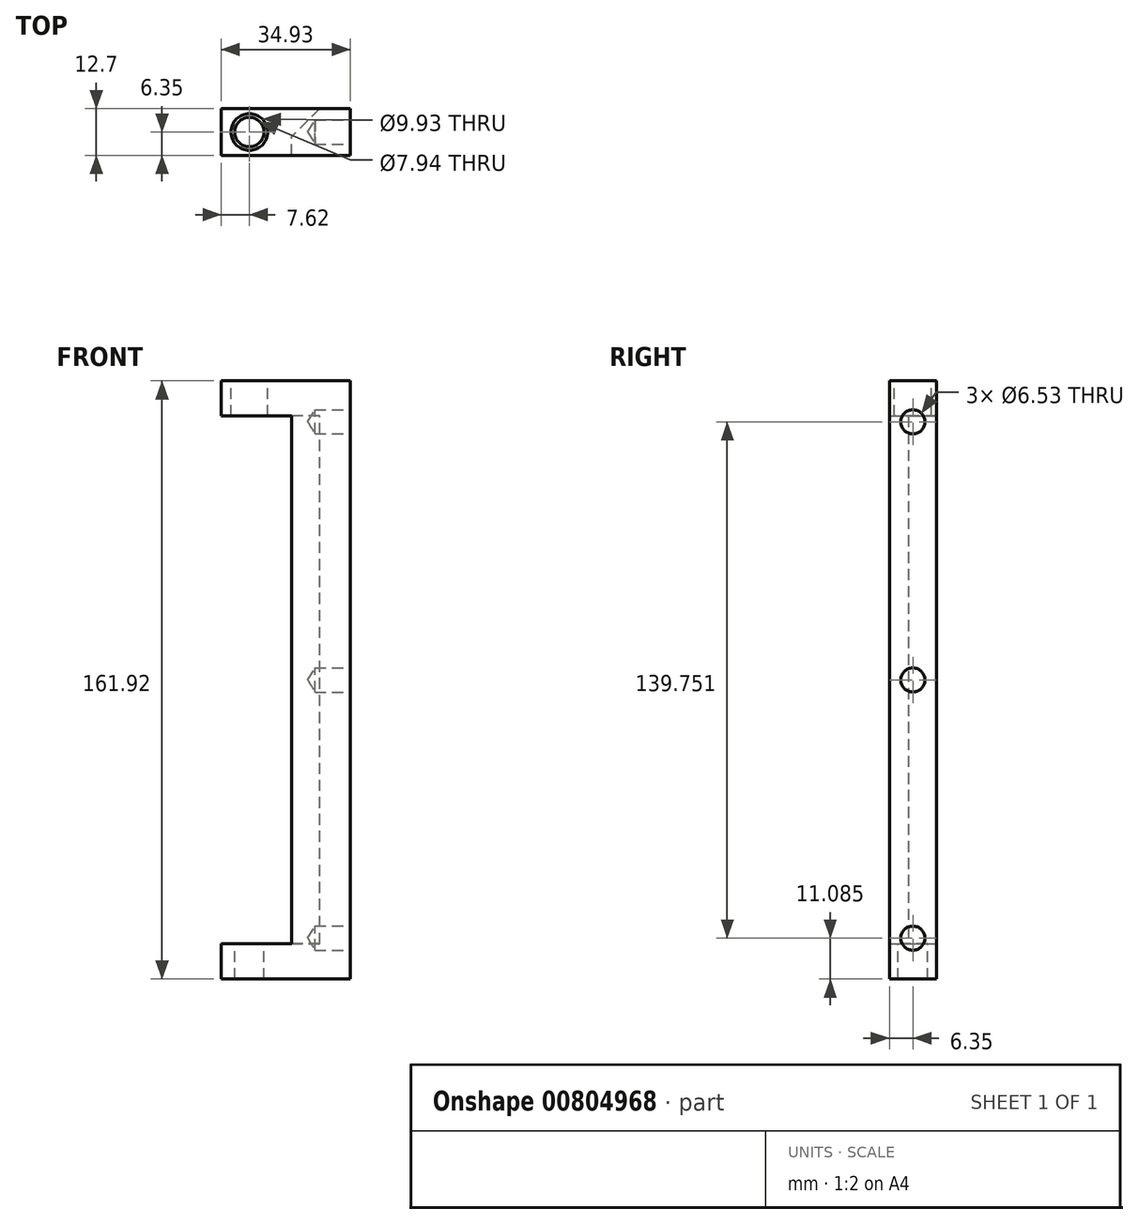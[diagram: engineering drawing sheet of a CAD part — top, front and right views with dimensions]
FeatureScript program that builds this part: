
annotation { "Feature Type Name" : "Feature", "Feature Type Description" : "" }
export const myFeature = defineFeature(function(context is Context, id is Id, definition is map)
    precondition{}
    {
        {
            var Q0;
            Q0=qCreatedBy(makeId("Front.planeOp"),FACE);
            var sketch = newSketch(context, id + "F0", { "sketchPlane" : qUnion([Q0])});
            skLineSegment(sketch, "E0", {"start": v(0, 11.43) * mm, "end": v(0, 71.44) * mm});
            skLineSegment(sketch, "E1", {"start": v(0, 71.44) * mm, "end": v(-19.05, 71.44) * mm});
            skLineSegment(sketch, "E2", {"start": v(-19.05, 71.44) * mm, "end": v(-19.05, 80.96) * mm});
            skLineSegment(sketch, "E3", {"start": v(-19.05, 80.96) * mm, "end": v(15.87, 80.96) * mm});
            skLineSegment(sketch, "E4", {"start": v(15.87, 80.96) * mm, "end": v(15.88, 0) * mm});
            skLineSegment(sketch, "E5", {"start": v(0, 0) * mm, "end": v(15.88, 0) * mm, "construction": true});
            skLineSegment(sketch, "E6.MirrorCS", {"start": v(0, -11.43) * mm, "end": v(0, -71.44) * mm});
            skLineSegment(sketch, "E7.MirrorCS", {"start": v(15.88, -80.96) * mm, "end": v(15.88, 0) * mm});
            skLineSegment(sketch, "E8.MirrorCS", {"start": v(-19.05, -71.44) * mm, "end": v(-19.05, -80.96) * mm});
            skLineSegment(sketch, "E9.MirrorCS", {"start": v(-19.05, -80.96) * mm, "end": v(15.88, -80.96) * mm});
            skLineSegment(sketch, "E10.MirrorCS", {"start": v(0, -71.44) * mm, "end": v(-19.05, -71.44) * mm});
            skLineSegment(sketch, "E11", {"start": v(0, 11.43) * mm, "end": v(-19.05, 11.43) * mm, "construction": true});
            skLineSegment(sketch, "E12", {"start": v(-19.05, 11.43) * mm, "end": v(-19.05, 0) * mm, "construction": true});
            skLineSegment(sketch, "E13.MirrorCS", {"start": v(0, -11.43) * mm, "end": v(-19.05, -11.43) * mm, "construction": true});
            skLineSegment(sketch, "E14.MirrorCS", {"start": v(-19.05, -11.43) * mm, "end": v(-19.05, 0) * mm, "construction": true});
            skPoint(sketch, "E15.orphan", {"position": v(0, 0) * mm});
            skLineSegment(sketch, "E16", {"start": v(0, 11.43) * mm, "end": v(0, -11.43) * mm});
            skSolve(sketch);
        }
        {
            var Q0;
            Q0 = qSketchRegion(id + "F0", true);
            extrude(context, id + "F1", {"entities" : qUnion([Q0]), "depth" : 12.7 * mm, "offsetDistance" : 25.4 * mm});
        }
        {
            var Q0;
            Q0=makeQuery(id+"F1.opExtrude","SWEPT_FACE",FACE,{"disambiguationData":[OSD([sQuery(id+"F0.wireOp",EDGE,"E3")])]});
            var sketch = newSketch(context, id + "F2", { "sketchPlane" : qUnion([Q0])});
            skPoint(sketch, "E17.centerSnap0", {"position": v(-19.05, -6.35) * mm});
            skPoint(sketch, "E18", {"position": v(-11.43, -6.35) * mm});
            skSolve(sketch);
        }
        {
            var Q0;
            Q0=makeQuery(id+"F1.opExtrude","CAP_EDGE",EDGE,{"disambiguationData":[OSD([sQuery(id+"F0.wireOp",EDGE,"E0")])],"isStart":true});
            chamfer(context, id + "F3", {"entities" : qUnion([Q0]), "chamferType" : ChamferType.OFFSET_ANGLE, "width" : 7.62 * mm, "oppositeDirection" : true, "angle" : 45 * degree, "tangentPropagation" : true});
        }
        {
            var Q0;
            Q0=makeQuery(id+"F1.opExtrude","SWEPT_FACE",FACE,{"disambiguationData":[OSD([sQuery(id+"F0.wireOp",EDGE,"E10.MirrorCS")])]});
            var sketch = newSketch(context, id + "F4", { "sketchPlane" : qUnion([Q0])});
            skPoint(sketch, "E19", {"position": v(-11.43, -6.35) * mm});
            skPoint(sketch, "E19.positionSnap0", {"position": v(-19.05, -6.35) * mm});
            skSolve(sketch);
        }
        {
            var Q0;
            Q0=sQuery(id+"F2.wireOp",VERTEX,"E18");
            var Q1;
            Q1=makeQuery(id+"F1.opExtrude","SWEPT_BODY",BODY,{"disambiguationData":[OSD([sQuery(id+"F0.wireOp",EDGE,"E0"),sQuery(id+"F0.wireOp",EDGE,"E1"),sQuery(id+"F0.wireOp",EDGE,"E2"),sQuery(id+"F0.wireOp",EDGE,"E3"),sQuery(id+"F0.wireOp",EDGE,"E4"),sQuery(id+"F0.wireOp",EDGE,"E6.MirrorCS"),sQuery(id+"F0.wireOp",EDGE,"E7.MirrorCS"),sQuery(id+"F0.wireOp",EDGE,"E8.MirrorCS"),sQuery(id+"F0.wireOp",EDGE,"E9.MirrorCS"),sQuery(id+"F0.wireOp",EDGE,"E10.MirrorCS"),sQuery(id+"F0.wireOp",EDGE,"E11"),sQuery(id+"F0.wireOp",EDGE,"E12"),sQuery(id+"F0.wireOp",EDGE,"E13.MirrorCS"),sQuery(id+"F0.wireOp",EDGE,"E14.MirrorCS")])]});
            hole(context, id + "F5", {"style" : HoleStyle.SIMPLE, "endStyle" : HoleEndStyle.BLIND, "standardTappedOrClearance" : lookupTablePath({ "fit" : "Close (ASME)", "standard" : "ANSI", "size" : "3/8", "type" : "Clearance" }), "standardBlindInLast" : lookupTablePath({ "fit" : "Close (ASME)", "standard" : "ANSI", "engagement" : "75%", "pitch" : "16 tpi", "size" : "3/8", "type" : "Clearance & tapped" }), "holeDiameter" : 9.93 * mm, "majorDiameter" : 7.94 * mm, "holeDepth" : 25.4 * mm, "isTappedThrough" : true, "tappedDepth" : 8.46 * mm, "tapClearance" : 3, "startFromSketch" : true, "locations" : qUnion([Q0]), "scope" : qUnion([Q1])});
        }
        {
            var Q0;
            Q0=sQuery(id+"F4.wireOp",VERTEX,"E19");
            var Q1;
            Q1=makeQuery(id+"F1.opExtrude","SWEPT_BODY",BODY,{"disambiguationData":[OSD([sQuery(id+"F0.wireOp",EDGE,"E0"),sQuery(id+"F0.wireOp",EDGE,"E1"),sQuery(id+"F0.wireOp",EDGE,"E2"),sQuery(id+"F0.wireOp",EDGE,"E3"),sQuery(id+"F0.wireOp",EDGE,"E4"),sQuery(id+"F0.wireOp",EDGE,"E6.MirrorCS"),sQuery(id+"F0.wireOp",EDGE,"E7.MirrorCS"),sQuery(id+"F0.wireOp",EDGE,"E8.MirrorCS"),sQuery(id+"F0.wireOp",EDGE,"E9.MirrorCS"),sQuery(id+"F0.wireOp",EDGE,"E10.MirrorCS"),sQuery(id+"F0.wireOp",EDGE,"E11"),sQuery(id+"F0.wireOp",EDGE,"E12"),sQuery(id+"F0.wireOp",EDGE,"E13.MirrorCS"),sQuery(id+"F0.wireOp",EDGE,"E14.MirrorCS")])]});
            hole(context, id + "F6", {"style" : HoleStyle.SIMPLE, "endStyle" : HoleEndStyle.THROUGH, "standardTappedOrClearance" : lookupTablePath({ "standard" : "ANSI", "engagement" : "75%", "pitch" : "16 tpi", "size" : "3/8", "type" : "Tapped" }), "standardBlindInLast" : lookupTablePath({ "standard" : "ANSI", "fit" : "Normal", "engagement" : "75%", "pitch" : "16 tpi", "size" : "3/8", "type" : "Clearance & tapped" }), "holeDiameter" : 7.94 * mm, "majorDiameter" : 9.52 * mm, "showTappedDepth" : true, "isTappedThrough" : true, "tappedDepth" : 2.12 * mm, "tapClearance" : 3, "startFromSketch" : true, "locations" : qUnion([Q0]), "scope" : qUnion([Q1])});
        }
        {
            var Q0;
            Q0=makeQuery(id+"F1.opExtrude","SWEPT_FACE",FACE,{"disambiguationData":[OSD([sQuery(id+"F0.wireOp",EDGE,"E4"),sQuery(id+"F0.wireOp",EDGE,"E7.MirrorCS")])]});
            var sketch = newSketch(context, id + "F7", { "sketchPlane" : qUnion([Q0])});
            skPoint(sketch, "E20", {"position": v(-6.35, -69.88) * mm});
            skPoint(sketch, "E20.positionSnap0", {"position": v(-6.35, -80.96) * mm});
            skPoint(sketch, "E21", {"position": v(-6.35, 0) * mm});
            skPoint(sketch, "E22", {"position": v(-6.35, 69.88) * mm});
            skCircle(sketch, "E23", {"center": v(-6.35, 69.88) * mm, "radius": 4.01 * mm, "construction": true});
            skCircle(sketch, "E24", {"center": v(-6.35, 0) * mm, "radius": 4.01 * mm, "construction": true});
            skCircle(sketch, "E25", {"center": v(-6.35, -69.88) * mm, "radius": 4.01 * mm, "construction": true});
            skSolve(sketch);
        }
        {
            var Q0;
            Q0=sQuery(id+"F7.wireOp",VERTEX,"E20");
            var Q1;
            Q1=sQuery(id+"F7.wireOp",VERTEX,"E21");
            var Q2;
            Q2=sQuery(id+"F7.wireOp",VERTEX,"E22");
            var Q3;
            Q3=makeQuery(id+"F1.opExtrude","SWEPT_BODY",BODY,{"disambiguationData":[OSD([sQuery(id+"F0.wireOp",EDGE,"E0"),sQuery(id+"F0.wireOp",EDGE,"E1"),sQuery(id+"F0.wireOp",EDGE,"E2"),sQuery(id+"F0.wireOp",EDGE,"E3"),sQuery(id+"F0.wireOp",EDGE,"E4"),sQuery(id+"F0.wireOp",EDGE,"E6.MirrorCS"),sQuery(id+"F0.wireOp",EDGE,"E7.MirrorCS"),sQuery(id+"F0.wireOp",EDGE,"E8.MirrorCS"),sQuery(id+"F0.wireOp",EDGE,"E9.MirrorCS"),sQuery(id+"F0.wireOp",EDGE,"E10.MirrorCS")])]});
            hole(context, id + "F8", {"style" : HoleStyle.SIMPLE, "endStyle" : HoleEndStyle.BLIND, "standardTappedOrClearance" : lookupTablePath({ "standard" : "ANSI", "engagement" : "75%", "pitch" : "18 tpi", "size" : "5/16", "type" : "Tapped" }), "standardBlindInLast" : lookupTablePath({ "standard" : "ANSI", "engagement" : "75%", "pitch" : "18 tpi", "size" : "5/16", "type" : "Tapped" }), "holeDiameter" : 6.53 * mm, "majorDiameter" : 7.94 * mm, "showTappedDepth" : true, "holeDepth" : 9.52 * mm, "isTappedThrough" : true, "tappedDepth" : 5.3 * mm, "tapClearance" : 3, "startFromSketch" : true, "locations" : qUnion([Q0, Q1, Q2]), "scope" : qUnion([Q3])});
        }
    });
